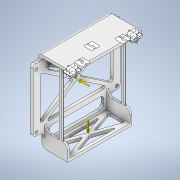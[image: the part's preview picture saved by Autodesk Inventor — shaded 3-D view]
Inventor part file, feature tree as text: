
AUTODESK INVENTOR PART (.ipt)
format: ipt  version: 2022 (Build 260153000, 153)  size: 840,704 bytes
history: native  units: in
note: dims shown in document units (in); Inventor stores cm internally (conversion verified against a paired STEP export)
features: fillet x18, sketch x17, extrude x15, mirror x3, hole x2, plane x1
ambient origin geometry x8: Origin, YZ Plane, XZ Plane, XY Plane, X Axis, Y Axis, Z Axis, Center Point
bodies: Solid1 (feature_tree)
feature tree (56):
  extrude  "Extrusion1"  Depth=1.3701in
  extrude  "Extrusion2"  Depth=1.252in
  plane  "Work Plane1"
  extrude  "Extrusion4"  Depth=0.1181in
  fillet  "Fillet1"  Radius=0.1181in
  mirror  "Mirror2"
  hole  "Hole2"  [1 undecoded]
  extrude  "Extrusion19"  Depth=0.1181in TaperAngle=0.0deg
  fillet  "Fillet14"  Radius=0.0394in
  extrude  "Extrusion20"  Depth=0.6339in
  fillet  "Fillet16"  Radius=0.1496in
  fillet  "Fillet17"  Radius=0.6339in
  hole  "Hole4"  [1 undecoded]
  extrude  "Extrusion24"  Depth=0.3937in
  fillet  "Fillet21"  Radius=0.3484in
  fillet  "Fillet22"  Radius=0.3937in
  fillet  "Fillet23"  Radius=3.0748in
  extrude  "Extrusion25"  Depth=0.2953in
  fillet  "Fillet24"  Radius=0.2992in
  extrude  "Extrusion26"  Depth=0.3937in
  mirror  "Mirror7"
  fillet  "Fillet25"  Radius=0.0557in
  fillet  "Fillet27"  Radius=0.1378in
  fillet  "Fillet28"  Radius=0.1378in
  extrude  "Extrusion27"  Depth=2.2913in
  extrude  "Extrusion28"  Depth=0.1378in
  extrude  "Extrusion29"  Depth=0.1378in
  extrude  "Extrusion30"  Depth=0.3937in TaperAngle=0.0deg
  extrude  "Extrusion31"  Depth=0.1575in
  fillet  "Fillet30"  Radius=0.0591in
  fillet  "Fillet31"  Radius=0.1575in
  fillet  "Fillet32"  Radius=2.4567in
  fillet  "Fillet35"  Radius=0.1496in
  extrude  "Extrusion33"  Depth=0.1575in TaperAngle=0.0deg
  fillet  "Fillet36"  Radius=0.1148in
  mirror  "Mirror9"
  fillet  "Fillet37"  Radius=0.1575in
  extrude  "Extrusion34"  Depth=0.1575in
  fillet  "Fillet38"  Radius=0.0394in
  sketch  "Sketch1"  dims[d0=1.3701in d1=2.9685in]
  sketch  "Sketch2"  dims[d2=1.6024in d3=0.0in d4=1.252in]
  sketch  "Sketch4"  dims[d5=1.4843in d6=0.0in d17=0.1181in d18=0.1181in]
  sketch  "Sketch22"  dims[d19=0.1457in d20=0.1575in]
  sketch  "Sketch24"  dims[d21=0.1102in d22=0.1181in d23=0.0in d24=0.0394in]
  sketch  "Sketch26"  dims[d80=0.2697in d126=0.6339in d127=0.1496in d128=0.6339in]
  sketch  "Sketch30"  dims[d129=0.124in d130=0.2362in d131=0.1575in d132=0.0787in d133=90.0deg d134=0.315in d135=0.8108in d170=3.6654in]
  sketch  "Sketch31"  dims[d171=2.649in d172=1.3695in d173=0.3484in d174=0.3937in d175=0.0in d192=3.0748in]
  sketch  "Sketch32"  dims[d193=1.9685in d194=0.2953in d195=0.2992in]
  sketch  "Sketch33"  dims[d196=0.3937in d197=0.0in d204=0.124in d205=0.124in d208=0.0557in d222=0.1378in d223=0.1378in]
  sketch  "Sketch34"  dims[d224=3.3898in d225=2.2913in]
  sketch  "Sketch35"  dims[d226=2.2913in d227=0.1378in]
  sketch  "Sketch36"  dims[d228=3.3898in d229=0.1378in]
  sketch  "Sketch37"  dims[d230=0.1299in d231=0.2362in d232=0.1575in d233=0.0787in d234=90.0deg d235=0.315in d236=0.8108in d238=0.3937in d239=0.0in]
  sketch  "Sketch38"  dims[d240=0.1575in d241=0.0787in d242=0.0591in d243=0.1575in d244=2.4567in d245=0.1496in]
  sketch  "Sketch40"  dims[d246=0.2559in d247=0.0787in d248=0.0in d249=0.1148in d250=0.1575in d251=0.0in]
  sketch  "Sketch41"  dims[d252=0.1181in d254=0.0394in d255=0.0394in d256=0.1181in d257=2.6969in d258=0.6457in d259=0.0in d260=0.1181in d261=0.9843in d262=0.0in d263=0.0787in d264=0.5276in d265=0.0787in d266=0.5276in d267=0.9843in d268=0.0in d270=0.7514in d271=2.4606in d272=0.1181in d273=0.9843in d274=0.0in d275=0.1181in d276=0.1181in d277=0.1181in d278=0.0591in d279=0.0591in d280=2.5787in d281=0.7514in d282=2.4606in d283=0.7514in d284=0.0591in d285=0.1738in d286=0.3937in d287=0.0in d288=0.0315in d289=0.0591in d290=0.1969in d296=0.3602in d298=0.2362in d299=0.1575in d300=0.0787in d301=0.9843in d302=0.0in d303=0.0354in d304=0.0354in d305=2.3031in d306=0.4941in d307=0.1181in d308=0.1181in d309=0.3937in d310=0.0in d311=0.1575in d105=0.0in d106=0.0in d107=0.0in d108=0.0in d119=0.0197in d120=0.0344in d121=0.0197in d122=0.0344in d143=0.0394in d144=0.0394in d145=0.0394in d146=0.0059in d147=0.1516in d148=0.0148in d149=0.5635in d150=0.0295in d151=0.8108in d152=0.0025in d153=0.0295in d154=0.0148in d166=0.0197in d167=0.0344in d168=0.0197in d169=0.0344in d209=0.0in d210=0.0in d211=0.0in d213=0.0197in d214=0.0344in d215=0.0197in d216=0.0344in]
note: 2 required parameter values undecoded (feature->parameter linkage not recoverable at this tier; creation-order binding heuristic only, values carry confidence <= 0.55)
